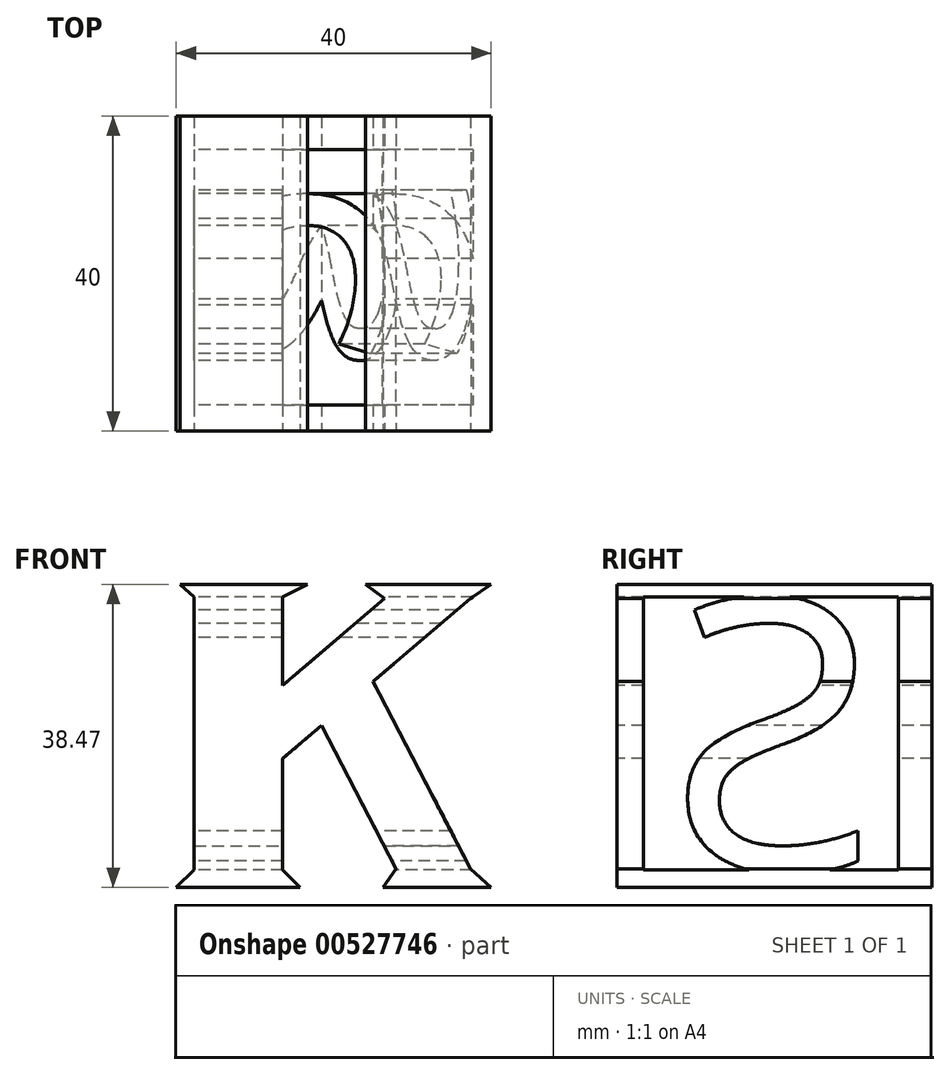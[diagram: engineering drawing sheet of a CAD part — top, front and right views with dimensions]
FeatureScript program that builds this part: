
annotation { "Feature Type Name" : "Feature", "Feature Type Description" : "" }
export const myFeature = defineFeature(function(context is Context, id is Id, definition is map)
    precondition{}
    {
        {
            var Q0;
            Q0=qCreatedBy(makeId("Top.planeOp"),FACE);
            var sketch = newSketch(context, id + "F0", { "sketchPlane" : qUnion([Q0])});
            skLineSegment(sketch, "E0.bottom", {"start": v(-18.45, 26.16) * mm, "end": v(21.55, 26.16) * mm});
            skLineSegment(sketch, "E0.top", {"start": v(-18.45, -13.84) * mm, "end": v(21.55, -13.84) * mm});
            skLineSegment(sketch, "E0.left", {"start": v(-18.45, 26.16) * mm, "end": v(-18.45, -13.84) * mm});
            skLineSegment(sketch, "E0.right", {"start": v(21.55, 26.16) * mm, "end": v(21.55, -13.84) * mm});
            skSolve(sketch);
        }
        {
            var Q0;
            Q0 = qSketchRegion(id + "F0", true);
            extrude(context, id + "F1", {"entities" : qUnion([Q0]), "endBound" : BoundingType.SYMMETRIC, "depth" : 40 * mm, "offsetDistance" : 25.4 * mm});
        }
        {
            var Q0;
            Q0=makeQuery(id+"F1.opExtrude","SWEPT_FACE",FACE,{"disambiguationData":[OSD([sQuery(id+"F0.wireOp",EDGE,"E0.top")])]});
            var sketch = newSketch(context, id + "F2", { "sketchPlane" : qUnion([Q0])});
            skLineSegment(sketch, "E1.bottom", {"start": v(-16.18, 16.92) * mm, "end": v(-4.92, 16.92) * mm});
            skLineSegment(sketch, "E1.top", {"start": v(-16.18, -17.76) * mm, "end": v(-4.92, -17.76) * mm});
            skLineSegment(sketch, "E1.left", {"start": v(-16.18, 16.92) * mm, "end": v(-16.18, -17.76) * mm});
            skLineSegment(sketch, "E1.right", {"start": v(-4.92, 16.92) * mm, "end": v(-4.92, -17.76) * mm});
            skLineSegment(sketch, "E2", {"start": v(-4.92, 5.66) * mm, "end": v(8.03, 16.7) * mm});
            skLineSegment(sketch, "E3", {"start": v(8.03, 16.7) * mm, "end": v(18.93, 16.7) * mm});
            skLineSegment(sketch, "E4", {"start": v(0, 0.56) * mm, "end": v(9.48, -17.64) * mm});
            skLineSegment(sketch, "E5", {"start": v(9.48, -17.64) * mm, "end": v(18.93, -17.64) * mm});
            skLineSegment(sketch, "E6", {"start": v(18.93, -17.64) * mm, "end": v(6.5, 6.2) * mm});
            skLineSegment(sketch, "E7", {"start": v(-1.75, 18.47) * mm, "end": v(-4.92, 16.92) * mm});
            skLineSegment(sketch, "E8", {"start": v(8.03, 16.7) * mm, "end": v(5.56, 18.47) * mm});
            skLineSegment(sketch, "E9", {"start": v(9.48, -17.64) * mm, "end": v(7.8, -20) * mm});
            skLineSegment(sketch, "E10", {"start": v(7.8, -20) * mm, "end": v(21.55, -20) * mm});
            skLineSegment(sketch, "E11", {"start": v(21.55, -20) * mm, "end": v(18.93, -17.64) * mm});
            skLineSegment(sketch, "E12", {"start": v(-16.18, -17.76) * mm, "end": v(-18.45, -20) * mm});
            skLineSegment(sketch, "E13", {"start": v(-4.92, -17.76) * mm, "end": v(-2.74, -20) * mm});
            skLineSegment(sketch, "E14", {"start": v(-2.74, -20) * mm, "end": v(-18.45, -20) * mm});
            skLineSegment(sketch, "E15", {"start": v(5.56, 18.47) * mm, "end": v(21.55, 18.47) * mm});
            skLineSegment(sketch, "E16", {"start": v(21.55, 18.47) * mm, "end": v(18.93, 16.7) * mm});
            skLineSegment(sketch, "E17", {"start": v(-16.18, 16.92) * mm, "end": v(-17.93, 18.47) * mm});
            skLineSegment(sketch, "E18", {"start": v(-17.93, 18.47) * mm, "end": v(-1.75, 18.47) * mm});
            skLineSegment(sketch, "E19", {"start": v(18.93, 16.7) * mm, "end": v(-4.92, -3.64) * mm});
            skSolve(sketch);
        }
        {
            var Q0;
            Q0=makeQuery(id+"F2.imprint","IMPRINT",FACE,{"disambiguationData":[TD([[makeQuery(id+"F2.imprint","IMPRINT",EDGE,{"derivedFrom":sQuery(id+"F2.wireOp",EDGE,"E1.left")}),-1.0]])]});
            var Q1;
            {var subQ2=sQuery(id+"F2.wireOp",EDGE,"E4");Q1=makeQuery(id+"F2.imprint","IMPRINT",FACE,{"disambiguationData":[TD([[makeQuery(id+"F2.imprint","IMPRINT",EDGE,{"derivedFrom":subQ2}),-1.0]])]});}
            var Q2;
            {var subQ4=sQuery(id+"F2.wireOp",EDGE,"E11");Q2=makeQuery(id+"F2.imprint","IMPRINT",FACE,{"disambiguationData":[TD([[makeQuery(id+"F2.imprint","IMPRINT",EDGE,{"derivedFrom":subQ4}),-1.0]])]});}
            extrude(context, id + "F3", {"entities" : qUnion([Q0, Q1, Q2]), "operationType" : NewBodyOperationType.REMOVE, "oppositeDirection" : true, "depth" : 40 * mm, "offsetDistance" : 25.4 * mm});
        }
        {
            var Q0;
            Q0=makeQuery(id+"F3.boolean.opBoolean","COPY",FACE,{"derivedFrom":makeQuery(id+"F3.opExtrude","SWEPT_FACE",FACE,{"disambiguationData":[OSD([sQuery(id+"F2.wireOp",EDGE,"E1.left")])]})});
            var sketch = newSketch(context, id + "F4", { "sketchPlane" : qUnion([Q0])});
            skLineSegment(sketch, "E20.bottom", {"start": v(-21.92, 16.92) * mm, "end": v(10.5, 16.92) * mm});
            skLineSegment(sketch, "E20.top", {"start": v(-21.92, -17.76) * mm, "end": v(10.5, -17.76) * mm});
            skLineSegment(sketch, "E20.left", {"start": v(-21.92, 16.92) * mm, "end": v(-21.92, -17.76) * mm});
            skLineSegment(sketch, "E20.right", {"start": v(10.5, 16.92) * mm, "end": v(10.5, -17.76) * mm});
            skText(sketch, "E21", { "text": "S", "fontName": "OpenSans-Regular.ttf"});
            const initialGuessF4  = {"E21": [-0.01925, -0.01776, 1, 0, 0.03468]};
            skSetInitialGuess(sketch, initialGuessF4);
            skSolve(sketch);
        }
        {
            var Q0;
            {var subQ1=sQuery(id+"F4.wireOp",EDGE,"E20.left");Q0=makeQuery(id+"F4.imprint","IMPRINT",FACE,{"disambiguationData":[TD([[makeQuery(id+"F4.imprint","IMPRINT",EDGE,{"derivedFrom":subQ1}),1.0]])]});}
            var Q1;
            {var subQ1=sQuery(id+"F4.wireOp",EDGE,"E20.right");Q1=makeQuery(id+"F4.imprint","IMPRINT",FACE,{"disambiguationData":[TD([[makeQuery(id+"F4.imprint","IMPRINT",EDGE,{"derivedFrom":subQ1}),-1.0]])]});}
            extrude(context, id + "F5", {"entities" : qUnion([Q0, Q1]), "operationType" : NewBodyOperationType.REMOVE, "oppositeDirection" : true, "depth" : 40 * mm, "offsetDistance" : 25.4 * mm});
        }
    });
